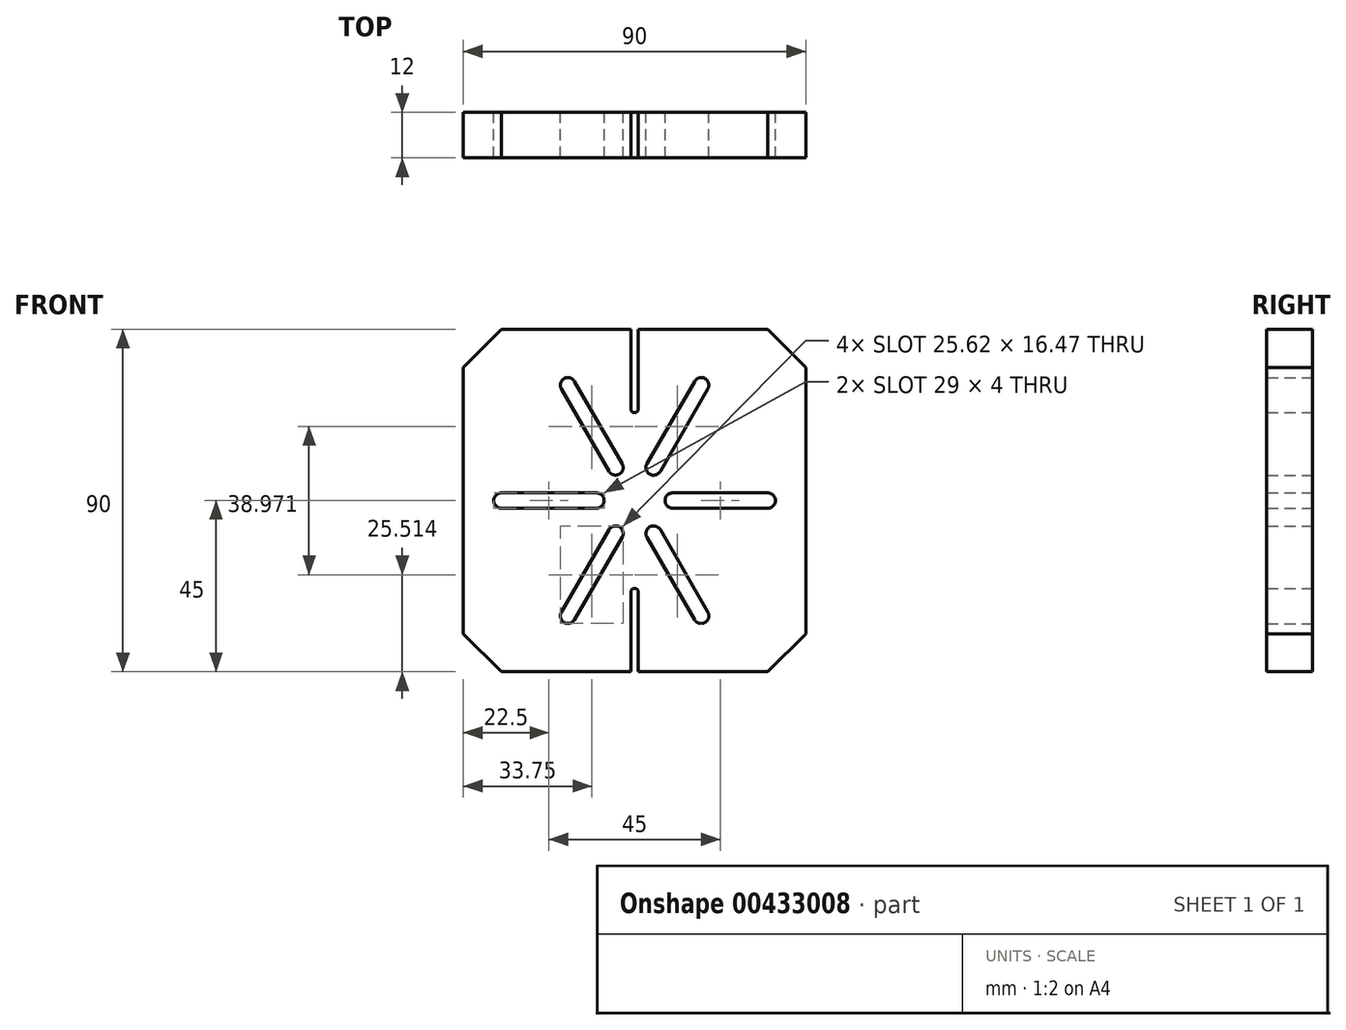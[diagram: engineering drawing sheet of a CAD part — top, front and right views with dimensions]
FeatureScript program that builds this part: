
annotation { "Feature Type Name" : "Feature", "Feature Type Description" : "" }
export const myFeature = defineFeature(function(context is Context, id is Id, definition is map)
    precondition{}
    {
        {
            var Q0;
            Q0=qCreatedBy(makeId("Front.planeOp"),FACE);
            var sketch = newSketch(context, id + "F0", { "sketchPlane" : qUnion([Q0])});
            skLineSegment(sketch, "E0.bottom", {"start": v(45, -45) * mm, "end": v(1, -45) * mm});
            skLineSegment(sketch, "E0.top", {"start": v(45, 45) * mm, "end": v(1, 45) * mm});
            skLineSegment(sketch, "E0.left", {"start": v(45, -45) * mm, "end": v(45, 45) * mm});
            skLineSegment(sketch, "E0.right", {"start": v(-45, -45) * mm, "end": v(-45, 45) * mm});
            skPoint(sketch, "E0.middle", {"position": v(0, 0) * mm});
            skArc(sketch, "E1.0.endCap", {"start": v(-1, -24.1) * mm, "mid": v(0, -23.1) * mm, "end": v(1, -24.1) * mm});
            skLineSegment(sketch, "E1.0.left", {"start": v(-1, -45) * mm, "end": v(-1, -24.1) * mm});
            skLineSegment(sketch, "E1.0.right", {"start": v(1, -45) * mm, "end": v(1, -24.1) * mm});
            skLineSegment(sketch, "E2", {"start": v(-1, -45) * mm, "end": v(-45, -45) * mm});
            skLineSegment(sketch, "E3.MirrorCS", {"start": v(-1, 45) * mm, "end": v(-1, 24.1) * mm});
            skArc(sketch, "E4.MirrorCS", {"start": v(-1, 24.1) * mm, "mid": v(0, 23.1) * mm, "end": v(1, 24.1) * mm});
            skLineSegment(sketch, "E5.MirrorCS", {"start": v(1, 45) * mm, "end": v(1, 24.1) * mm});
            skLineSegment(sketch, "E6", {"start": v(-0.92, 45) * mm, "end": v(-45, 45) * mm});
            skLineSegment(sketch, "E7", {"start": v(-10, 0) * mm, "end": v(-35, 0) * mm});
            skArc(sketch, "E8.0.startCap", {"start": v(-10, 2) * mm, "mid": v(-8, 0) * mm, "end": v(-10, -2) * mm});
            skArc(sketch, "E8.0.endCap", {"start": v(-35, -2) * mm, "mid": v(-37, 0) * mm, "end": v(-35, 2) * mm});
            skLineSegment(sketch, "E8.0.left", {"start": v(-10, -2) * mm, "end": v(-35, -2) * mm});
            skLineSegment(sketch, "E8.0.right", {"start": v(-10, 2) * mm, "end": v(-35, 2) * mm});
            skLineSegment(sketch, "E9.1.0", {"start": v(-3.27, -9.66) * mm, "end": v(-15.77, -31.31) * mm});
            skArc(sketch, "E9.1.1", {"start": v(-15.77, -31.31) * mm, "mid": v(-18.5, -32.04) * mm, "end": v(-19.23, -29.31) * mm});
            skArc(sketch, "E9.1.2", {"start": v(-6.73, -7.66) * mm, "mid": v(-4, -6.93) * mm, "end": v(-3.27, -9.66) * mm});
            skLineSegment(sketch, "E9.1.3", {"start": v(-5, -8.66) * mm, "end": v(-17.5, -30.31) * mm});
            skLineSegment(sketch, "E9.1.4", {"start": v(-6.73, -7.66) * mm, "end": v(-19.23, -29.31) * mm});
            skLineSegment(sketch, "E9.2.0", {"start": v(6.73, -7.66) * mm, "end": v(19.23, -29.31) * mm});
            skArc(sketch, "E9.2.1", {"start": v(19.23, -29.31) * mm, "mid": v(18.5, -32.04) * mm, "end": v(15.77, -31.31) * mm});
            skArc(sketch, "E9.2.2", {"start": v(3.27, -9.66) * mm, "mid": v(4, -6.93) * mm, "end": v(6.73, -7.66) * mm});
            skLineSegment(sketch, "E9.2.3", {"start": v(5, -8.66) * mm, "end": v(17.5, -30.31) * mm});
            skLineSegment(sketch, "E9.2.4", {"start": v(3.27, -9.66) * mm, "end": v(15.77, -31.31) * mm});
            skLineSegment(sketch, "E9.3.0", {"start": v(10, 2) * mm, "end": v(35, 2) * mm});
            skArc(sketch, "E9.3.1", {"start": v(35, 2) * mm, "mid": v(37, 0) * mm, "end": v(35, -2) * mm});
            skArc(sketch, "E9.3.2", {"start": v(10, -2) * mm, "mid": v(8, 0) * mm, "end": v(10, 2) * mm});
            skLineSegment(sketch, "E9.3.3", {"start": v(10, 0) * mm, "end": v(35, 0) * mm});
            skLineSegment(sketch, "E9.3.4", {"start": v(10, -2) * mm, "end": v(35, -2) * mm});
            skLineSegment(sketch, "E9.4.0", {"start": v(3.27, 9.66) * mm, "end": v(15.77, 31.31) * mm});
            skArc(sketch, "E9.4.1", {"start": v(15.77, 31.31) * mm, "mid": v(18.5, 32.04) * mm, "end": v(19.23, 29.31) * mm});
            skArc(sketch, "E9.4.2", {"start": v(6.73, 7.66) * mm, "mid": v(4, 6.93) * mm, "end": v(3.27, 9.66) * mm});
            skLineSegment(sketch, "E9.4.3", {"start": v(5, 8.66) * mm, "end": v(17.5, 30.31) * mm});
            skLineSegment(sketch, "E9.4.4", {"start": v(6.73, 7.66) * mm, "end": v(19.23, 29.31) * mm});
            skLineSegment(sketch, "E9.5.0", {"start": v(-6.73, 7.66) * mm, "end": v(-19.23, 29.31) * mm});
            skArc(sketch, "E9.5.1", {"start": v(-19.23, 29.31) * mm, "mid": v(-18.5, 32.04) * mm, "end": v(-15.77, 31.31) * mm});
            skArc(sketch, "E9.5.2", {"start": v(-3.27, 9.66) * mm, "mid": v(-4, 6.93) * mm, "end": v(-6.73, 7.66) * mm});
            skLineSegment(sketch, "E9.5.3", {"start": v(-5, 8.66) * mm, "end": v(-17.5, 30.31) * mm});
            skLineSegment(sketch, "E9.5.4", {"start": v(-3.27, 9.66) * mm, "end": v(-15.77, 31.31) * mm});
            skSolve(sketch);
        }
        {
            var Q0;
            Q0=makeQuery(id+"F0.imprint","IMPRINT",FACE,{"disambiguationData":[TD([[makeQuery(id+"F0.imprint","IMPRINT",EDGE,{"derivedFrom":sQuery(id+"F0.wireOp",EDGE,"E0.bottom")}),-1.0]])]});
            extrude(context, id + "F1", {"entities" : qUnion([Q0]), "depth" : 12 * mm, "offsetDistance" : 25 * mm});
        }
        {
            var Q0;
            Q0=makeQuery(id+"F1.opExtrude","SWEPT_EDGE",EDGE,{"disambiguationData":[OSD([sQuery(id+"F0.wireOp",EDGE,"E0.top"),sQuery(id+"F0.wireOp",EDGE,"E0.left")])]});
            var Q1;
            Q1=makeQuery(id+"F1.opExtrude","SWEPT_EDGE",EDGE,{"disambiguationData":[OSD([sQuery(id+"F0.wireOp",EDGE,"E0.bottom"),sQuery(id+"F0.wireOp",EDGE,"E0.left")])]});
            var Q2;
            Q2=makeQuery(id+"F1.opExtrude","SWEPT_EDGE",EDGE,{"disambiguationData":[OSD([sQuery(id+"F0.wireOp",EDGE,"E0.right"),sQuery(id+"F0.wireOp",EDGE,"E6")])]});
            var Q3;
            Q3=makeQuery(id+"F1.opExtrude","SWEPT_EDGE",EDGE,{"disambiguationData":[OSD([sQuery(id+"F0.wireOp",EDGE,"E0.right"),sQuery(id+"F0.wireOp",EDGE,"E2")])]});
            chamfer(context, id + "F2", {"entities" : qUnion([Q0, Q1, Q2, Q3]), "width" : 10 * mm, "tangentPropagation" : true});
        }
    });
